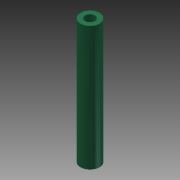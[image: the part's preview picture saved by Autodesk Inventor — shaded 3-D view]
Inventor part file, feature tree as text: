
AUTODESK INVENTOR PART (.ipt)
format: ipt  version: 2015 (Build 190159000, 159)  size: 72,704 bytes
history: native  units: in
note: dims shown in document units (in); Inventor stores cm internally (conversion verified against a paired STEP export)
features: extrude x1, sketch x1
ambient origin geometry x8: Origin, YZ Plane, XZ Plane, XY Plane, X Axis, Y Axis, Z Axis, Center Point
bodies: Solid1 (feature_tree)
feature tree (2):
  extrude  "Extrusion1"  Depth=1.9685in
  sketch  "Sketch1"  dims[d0=0.3in d1=0.155in d2=1.9685in d3=0.0in]
